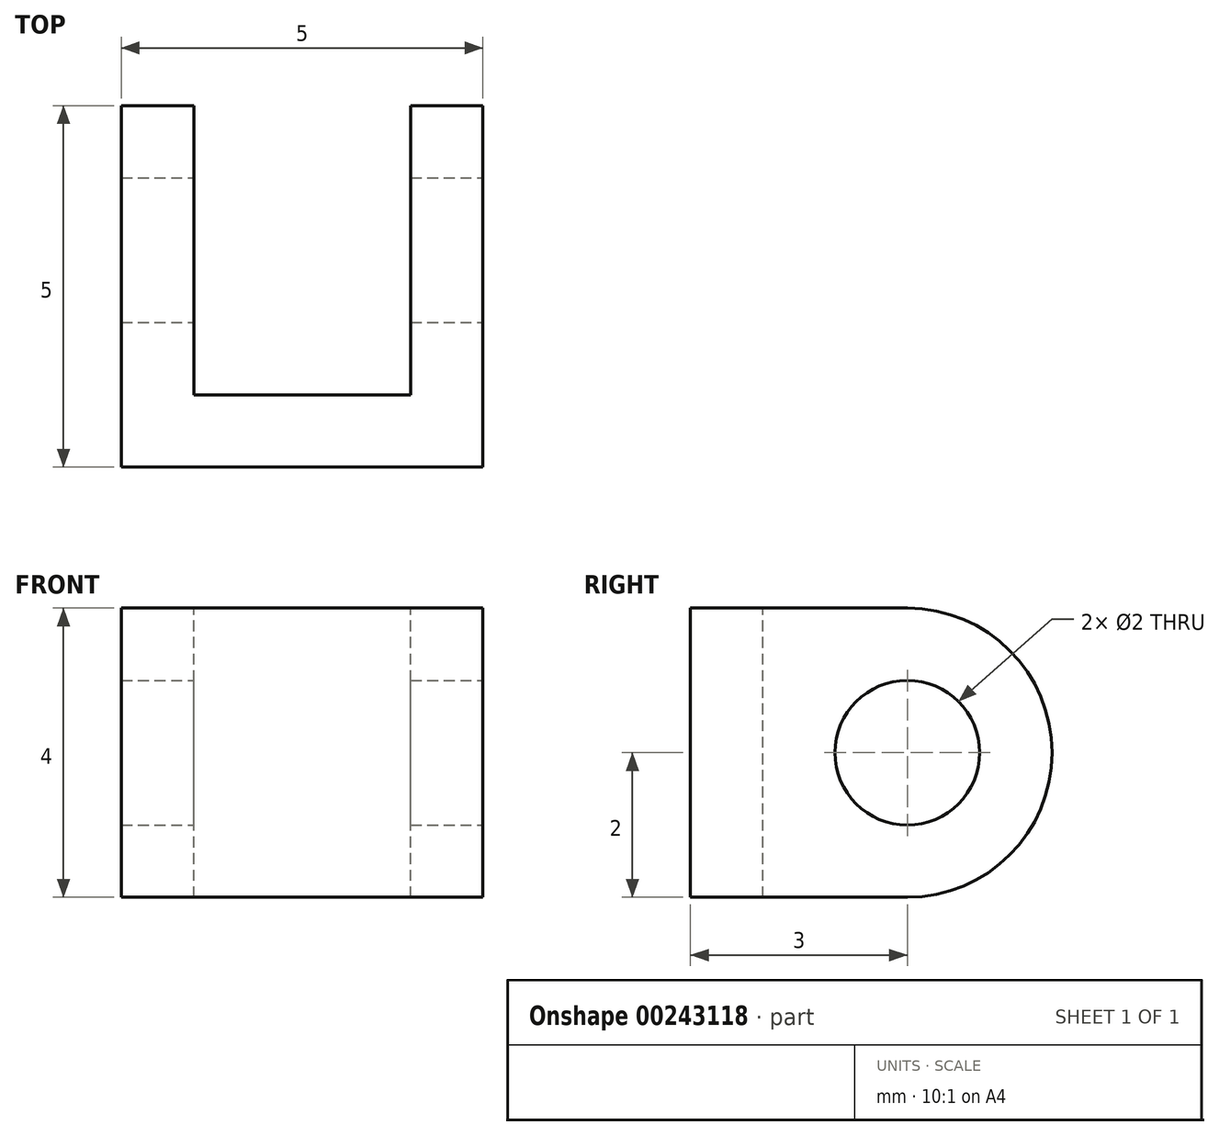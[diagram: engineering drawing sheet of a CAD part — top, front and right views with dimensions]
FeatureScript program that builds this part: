
annotation { "Feature Type Name" : "Feature", "Feature Type Description" : "" }
export const myFeature = defineFeature(function(context is Context, id is Id, definition is map)
    precondition{}
    {
        {
            var Q0;
            Q0=qCreatedBy(makeId("Top.planeOp"),FACE);
            var sketch = newSketch(context, id + "F0", { "sketchPlane" : qUnion([Q0])});
            skLineSegment(sketch, "E0", {"start": v(0, 0) * mm, "end": v(5, 0) * mm});
            skLineSegment(sketch, "E1", {"start": v(5, 0) * mm, "end": v(5, 5) * mm});
            skLineSegment(sketch, "E2", {"start": v(5, 5) * mm, "end": v(0, 5) * mm});
            skLineSegment(sketch, "E3", {"start": v(0, 5) * mm, "end": v(0, 0) * mm});
            skSolve(sketch);
        }
        {
            var Q0;
            Q0 = qSketchRegion(id + "F0", true);
            extrude(context, id + "F1", {"entities" : qUnion([Q0]), "depth" : 4 * mm});
        }
        {
            var Q0;
            Q0=makeQuery(id+"F1.opExtrude","SWEPT_FACE",FACE,{"disambiguationData":[OSD([sQuery(id+"F0.wireOp",EDGE,"E1")])]});
            var sketch = newSketch(context, id + "F2", { "sketchPlane" : qUnion([Q0])});
            skLineSegment(sketch, "E4", {"start": v(0, 4) * mm, "end": v(3, 4) * mm});
            skLineSegment(sketch, "E5", {"start": v(3, 4) * mm, "end": v(3, 2) * mm});
            skCircle(sketch, "E6", {"center": v(3, 2) * mm, "radius": 2 * mm});
            skSolve(sketch);
        }
        {
            var Q0;
            {var subQ0=sQuery(id+"F2.wireOp",EDGE,"E6");var subQ1=sQuery(id+"F0.wireOp",EDGE,"E1");var subQ2=makeQuery(id+"F1.opExtrude","CAP_EDGE",EDGE,{"disambiguationData":[OSD([subQ1])],"isStart":false});var subQ3=makeQuery(id+"F2.imprint","INTERSECT",VERTEX,{"derivedFrom":[subQ2,sQuery(id+"F2.wireOp",EDGE,"E4"),subQ0]});Q0=makeQuery(id+"F2.imprint","IMPRINT",FACE,{"disambiguationData":[TD([[makeQuery(id+"F2.imprint","IMPRINT",EDGE,{"disambiguationData":[TD([[subQ3,1.0]])],"derivedFrom":subQ0}),-1.0]])]});}
            var Q1;
            {var subQ0=sQuery(id+"F2.wireOp",EDGE,"E6");var subQ1=sQuery(id+"F0.wireOp",EDGE,"E1");var subQ4=makeQuery(id+"F1.opExtrude","CAP_EDGE",EDGE,{"disambiguationData":[OSD([subQ1])],"isStart":true});var subQ5=makeQuery(id+"F2.imprint","INTERSECT",VERTEX,{"derivedFrom":[subQ4,subQ0]});Q1=makeQuery(id+"F2.imprint","IMPRINT",FACE,{"disambiguationData":[TD([[makeQuery(id+"F2.imprint","IMPRINT",EDGE,{"disambiguationData":[TD([[subQ5,-1.0]])],"derivedFrom":subQ0}),-1.0]])]});}
            extrude(context, id + "F3", {"entities" : qUnion([Q0, Q1]), "operationType" : NewBodyOperationType.REMOVE, "oppositeDirection" : true, "depth" : 25 * mm});
        }
        {
            var Q0;
            Q0=makeQuery(id+"F1.opExtrude","CAP_FACE",FACE,{"disambiguationData":[OSD([sQuery(id+"F0.wireOp",EDGE,"E0"),sQuery(id+"F0.wireOp",EDGE,"E1"),sQuery(id+"F0.wireOp",EDGE,"E2"),sQuery(id+"F0.wireOp",EDGE,"E3")])],"isStart":false});
            var sketch = newSketch(context, id + "F4", { "sketchPlane" : qUnion([Q0])});
            skLineSegment(sketch, "E7", {"start": v(0, 0) * mm, "end": v(1, 0) * mm});
            skLineSegment(sketch, "E8", {"start": v(1, 0) * mm, "end": v(1, 1) * mm});
            skLineSegment(sketch, "E9", {"start": v(1, 1) * mm, "end": v(1, 5) * mm});
            skLineSegment(sketch, "E10", {"start": v(1, 1) * mm, "end": v(4, 1) * mm});
            skLineSegment(sketch, "E11", {"start": v(4, 1) * mm, "end": v(4, 5) * mm});
            skSolve(sketch);
        }
        {
            var Q0;
            {var subQ0=sQuery(id+"F4.wireOp",EDGE,"E10");Q0=makeQuery(id+"F4.imprint","IMPRINT",FACE,{"disambiguationData":[TD([[makeQuery(id+"F4.imprint","IMPRINT",EDGE,{"derivedFrom":subQ0}),1.0]])]});}
            extrude(context, id + "F5", {"entities" : qUnion([Q0]), "operationType" : NewBodyOperationType.REMOVE, "oppositeDirection" : true, "depth" : 5 * mm});
        }
        {
            var Q0;
            Q0=makeQuery(id+"F1.opExtrude","CAP_FACE",FACE,{"disambiguationData":[OSD([sQuery(id+"F0.wireOp",EDGE,"E0"),sQuery(id+"F0.wireOp",EDGE,"E1"),sQuery(id+"F0.wireOp",EDGE,"E2"),sQuery(id+"F0.wireOp",EDGE,"E3")])],"isStart":false});
            var sketch = newSketch(context, id + "F6", { "sketchPlane" : qUnion([Q0])});
            skLineSegment(sketch, "E12", {"start": v(1, 3) * mm, "end": v(1, 5) * mm});
            skLineSegment(sketch, "E13", {"start": v(4, 3) * mm, "end": v(4, 5) * mm});
            skLineSegment(sketch, "E14", {"start": v(1, 5) * mm, "end": v(4, 5) * mm});
            skLineSegment(sketch, "E15", {"start": v(1, 3) * mm, "end": v(4, 3) * mm});
            skSolve(sketch);
        }
        {
            var Q0;
            Q0=makeQuery(id+"F6.imprint","IMPRINT",FACE,{"disambiguationData":[TD([[makeQuery(id+"F6.imprint","IMPRINT",EDGE,{"derivedFrom":sQuery(id+"F6.wireOp",EDGE,"E12")}),-1.0]])]});
            extrude(context, id + "F7", {"entities" : qUnion([Q0]), "operationType" : NewBodyOperationType.REMOVE, "oppositeDirection" : true, "depth" : 5 * mm});
        }
        {
            var Q0;
            Q0=makeQuery(id+"F1.opExtrude","SWEPT_FACE",FACE,{"disambiguationData":[OSD([sQuery(id+"F0.wireOp",EDGE,"E1")])]});
            var sketch = newSketch(context, id + "F8", { "sketchPlane" : qUnion([Q0])});
            skLineSegment(sketch, "E16", {"start": v(0, 4) * mm, "end": v(0, 2) * mm});
            skLineSegment(sketch, "E17", {"start": v(0, 2) * mm, "end": v(3, 2) * mm});
            skCircle(sketch, "E18", {"center": v(3, 2) * mm, "radius": 1 * mm});
            skSolve(sketch);
        }
        {
            var Q0;
            Q0=makeQuery(id+"F8.imprint","IMPRINT",FACE,{"disambiguationData":[TD([[makeQuery(id+"F8.imprint","IMPRINT",EDGE,{"derivedFrom":sQuery(id+"F8.wireOp",EDGE,"E18")}),1.0]])]});
            extrude(context, id + "F9", {"entities" : qUnion([Q0]), "operationType" : NewBodyOperationType.REMOVE, "oppositeDirection" : true, "depth" : 25 * mm});
        }
    });
